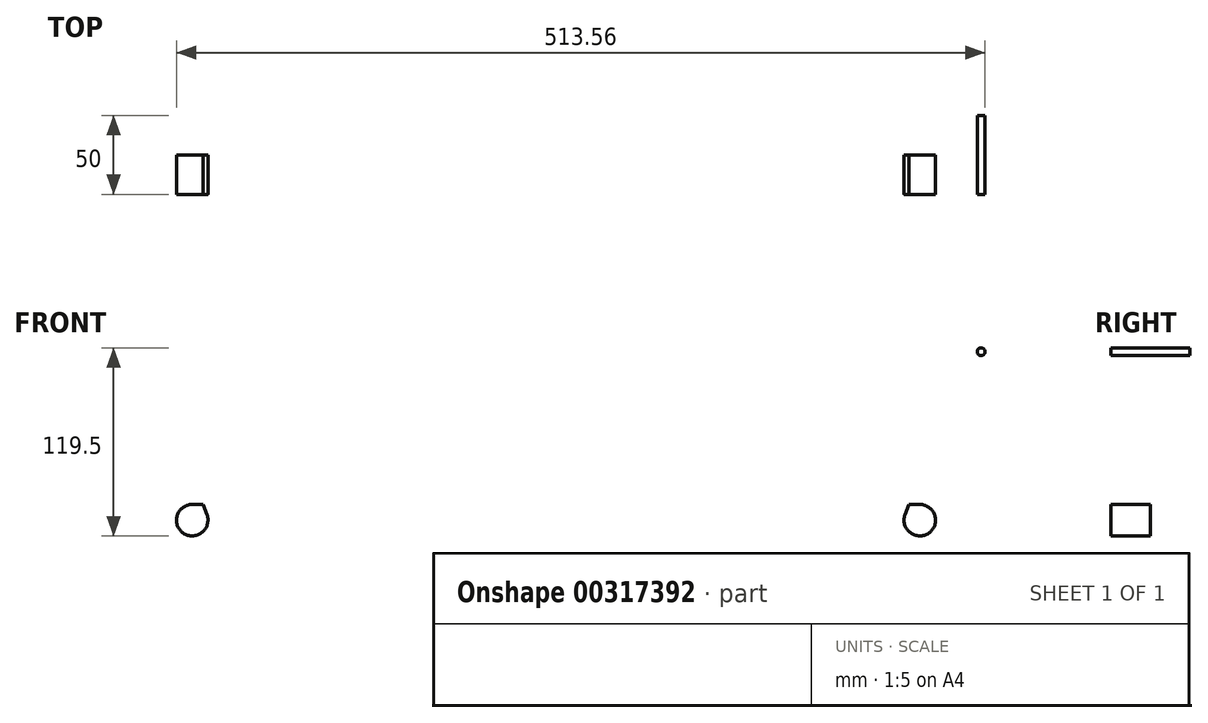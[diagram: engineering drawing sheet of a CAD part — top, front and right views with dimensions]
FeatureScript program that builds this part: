
annotation { "Feature Type Name" : "Feature", "Feature Type Description" : "" }
export const myFeature = defineFeature(function(context is Context, id is Id, definition is map)
    precondition{}
    {
        {
            var Q0;
            Q0=qCreatedBy(makeId("Front.planeOp"),FACE);
            var sketch = newSketch(context, id + "F0", { "sketchPlane" : qUnion([Q0])});
            skLineSegment(sketch, "E0", {"start": v(0, 0) * mm, "end": v(231.06, 0) * mm});
            skLineSegment(sketch, "E1", {"start": v(270, 107) * mm, "end": v(231.06, 0) * mm});
            skArc(sketch, "E2.0.startCap", {"start": v(0, -10) * mm, "mid": v(-10, 0) * mm, "end": v(0, 10) * mm});
            skArc(sketch, "E2.0.endCap", {"start": v(231.06, 10) * mm, "mid": v(241.06, 0) * mm, "end": v(231.06, -10) * mm});
            skLineSegment(sketch, "E2.0.left", {"start": v(0, 10) * mm, "end": v(231.06, 10) * mm});
            skLineSegment(sketch, "E2.0.right", {"start": v(0, -10) * mm, "end": v(231.06, -10) * mm});
            skArc(sketch, "E2.1.startCap", {"start": v(240.45, -3.42) * mm, "mid": v(227.63, -9.4) * mm, "end": v(221.66, 3.42) * mm});
            skArc(sketch, "E2.1.endCap", {"start": v(260.6, 110.42) * mm, "mid": v(273.42, 116.4) * mm, "end": v(279.4, 103.58) * mm});
            skLineSegment(sketch, "E2.1.left", {"start": v(260.6, 110.42) * mm, "end": v(221.66, 3.42) * mm});
            skLineSegment(sketch, "E2.1.right", {"start": v(279.4, 103.58) * mm, "end": v(240.45, -3.42) * mm});
            skCircle(sketch, "E3", {"center": v(270, 107) * mm, "radius": 2.5 * mm});
            skCircle(sketch, "E4", {"center": v(120, 0) * mm, "radius": 2.5 * mm});
            skSolve(sketch);
        }
        {
            var Q0;
            {var subQ4=sQuery(id+"F0.wireOp",EDGE,"E2.0.startCap");Q0=makeQuery(id+"F0.imprint","IMPRINT",FACE,{"disambiguationData":[TD([[makeQuery(id+"F0.imprint","IMPRINT",EDGE,{"derivedFrom":subQ4}),-1.0]])]});}
            var Q1;
            {var subQ4=sQuery(id+"F0.wireOp",EDGE,"E1");var subQ6=sQuery(id+"F0.wireOp",EDGE,"E0");var subQ7=makeQuery(id+"F0.imprint","INTERSECT",VERTEX,{"derivedFrom":[subQ6,subQ4]});Q1=makeQuery(id+"F0.imprint","IMPRINT",FACE,{"disambiguationData":[TD([[makeQuery(id+"F0.imprint","IMPRINT",EDGE,{"disambiguationData":[TD([[subQ7,1.0]])],"derivedFrom":subQ6}),-1.0]])]});}
            var Q2;
            {var subQ0=sQuery(id+"F0.wireOp",EDGE,"E2.1.endCap");Q2=makeQuery(id+"F0.imprint","IMPRINT",FACE,{"disambiguationData":[TD([[makeQuery(id+"F0.imprint","IMPRINT",EDGE,{"derivedFrom":subQ0}),-1.0]])]});}
            var Q3;
            {var subQ3=sQuery(id+"F0.wireOp",EDGE,"E1");var subQ7=sQuery(id+"F0.wireOp",EDGE,"E0");var subQ8=makeQuery(id+"F0.imprint","INTERSECT",VERTEX,{"derivedFrom":[subQ7,subQ3]});Q3=makeQuery(id+"F0.imprint","IMPRINT",FACE,{"disambiguationData":[TD([[makeQuery(id+"F0.imprint","IMPRINT",EDGE,{"disambiguationData":[TD([[subQ8,1.0]])],"derivedFrom":subQ7}),1.0]])]});}
            var Q4;
            Q4=makeQuery(id+"F0.imprint","IMPRINT",FACE,{"disambiguationData":[TD([[makeQuery(id+"F0.imprint","IMPRINT",EDGE,{"derivedFrom":sQuery(id+"F0.wireOp",EDGE,"E3")}),1.0]])]});
            var Q5;
            {var subQ0=sQuery(id+"F0.wireOp",EDGE,"E4");var subQ1=sQuery(id+"F0.wireOp",EDGE,"E0");var subQ2=makeQuery(id+"F0.imprint","INTERSECT",VERTEX,{"disambiguationData":[OD(0.0)],"derivedFrom":[subQ1,subQ0]});Q5=makeQuery(id+"F0.imprint","IMPRINT",FACE,{"disambiguationData":[TD([[makeQuery(id+"F0.imprint","IMPRINT",EDGE,{"disambiguationData":[TD([[subQ2,-1.0]])],"derivedFrom":subQ1}),-1.0]])]});}
            var Q6;
            {var subQ0=sQuery(id+"F0.wireOp",EDGE,"E4");var subQ1=sQuery(id+"F0.wireOp",EDGE,"E0");var subQ2=makeQuery(id+"F0.imprint","INTERSECT",VERTEX,{"disambiguationData":[OD(0.0)],"derivedFrom":[subQ1,subQ0]});Q6=makeQuery(id+"F0.imprint","IMPRINT",FACE,{"disambiguationData":[TD([[makeQuery(id+"F0.imprint","IMPRINT",EDGE,{"disambiguationData":[TD([[subQ2,-1.0]])],"derivedFrom":subQ1}),1.0]])]});}
            extrude(context, id + "F1", {"entities" : qUnion([Q0, Q1, Q2, Q3, Q4, Q5, Q6]), "depth" : 50 * mm});
        }
        {
            var Q0;
            Q0=qSketchRegion(id+"F0",true);
            var Q1;
            Q1=sQuery(id+"F0.wireOp",EDGE,"E4");
            var Q2;
            Q2=sQuery(id+"F0.wireOp",EDGE,"E3");
            extrude(context, id + "F2", {"entities" : qUnion([Q0]), "operationType" : NewBodyOperationType.REMOVE, "surfaceEntities" : qUnion([Q1, Q2]), "depth" : 25 * mm});
        }
        {
            var Q0;
            Q0=makeQuery(id+"F1.opExtrude","SWEPT_BODY",BODY,{"disambiguationData":[OSD([sQuery(id+"F0.wireOp",EDGE,"E2.0.startCap"),sQuery(id+"F0.wireOp",EDGE,"E2.0.left"),sQuery(id+"F0.wireOp",EDGE,"E2.0.right"),sQuery(id+"F0.wireOp",EDGE,"E2.1.startCap"),sQuery(id+"F0.wireOp",EDGE,"E2.1.endCap"),sQuery(id+"F0.wireOp",EDGE,"E2.1.left"),sQuery(id+"F0.wireOp",EDGE,"E2.1.right")])]});
            var Q1;
            Q1=qCreatedBy(makeId("Right.planeOp"),FACE);
            mirror(context, id + "F3", {"operationType" : NewBodyOperationType.ADD, "entities" : qUnion([Q0]), "mirrorPlane" : qUnion([Q1])});
        }
        {
            var Q0;
            Q0=makeQuery(id+"F1.opExtrude","SWEPT_BODY",BODY,{"disambiguationData":[OSD([sQuery(id+"F0.wireOp",EDGE,"E2.0.startCap"),sQuery(id+"F0.wireOp",EDGE,"E2.0.left"),sQuery(id+"F0.wireOp",EDGE,"E2.0.right"),sQuery(id+"F0.wireOp",EDGE,"E2.1.startCap"),sQuery(id+"F0.wireOp",EDGE,"E2.1.endCap"),sQuery(id+"F0.wireOp",EDGE,"E2.1.left"),sQuery(id+"F0.wireOp",EDGE,"E2.1.right")])]});
            transform(context, id + "F4", {"entities" : qUnion([Q0]), "transformType" : TransformType.TRANSLATION_3D, "dx" : 0 * mm, "dy" : 0 * mm, "dz" : 0 * mm, "makeCopy" : true});
        }
        {
            var Q0;
            Q0=makeQuery(id+"F4.opPattern","COPY",BODY,{"derivedFrom":makeQuery(id+"F1.opExtrude","SWEPT_BODY",BODY,{"disambiguationData":[OSD([sQuery(id+"F0.wireOp",EDGE,"E2.0.startCap"),sQuery(id+"F0.wireOp",EDGE,"E2.0.left"),sQuery(id+"F0.wireOp",EDGE,"E2.0.right"),sQuery(id+"F0.wireOp",EDGE,"E2.1.startCap"),sQuery(id+"F0.wireOp",EDGE,"E2.1.endCap"),sQuery(id+"F0.wireOp",EDGE,"E2.1.left"),sQuery(id+"F0.wireOp",EDGE,"E2.1.right")])]}),"instanceName":"1"});
            deleteBodies(context, id + "F5", {"entities" : qUnion([Q0])});
        }
    });
